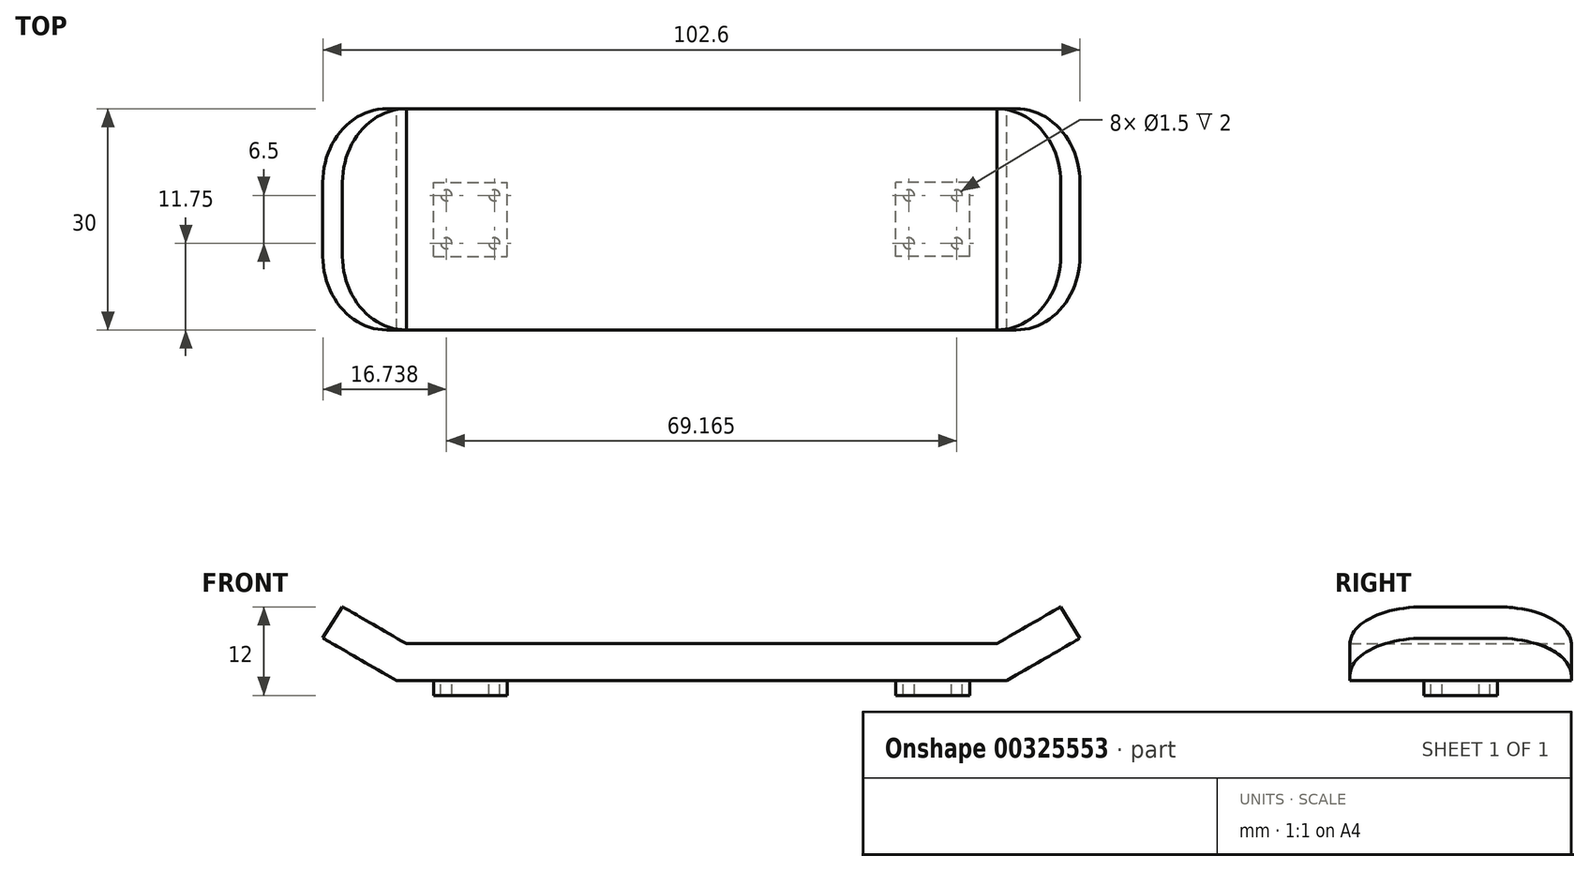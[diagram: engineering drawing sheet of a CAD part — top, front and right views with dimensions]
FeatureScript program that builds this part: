
annotation { "Feature Type Name" : "Feature", "Feature Type Description" : "" }
export const myFeature = defineFeature(function(context is Context, id is Id, definition is map)
    precondition{}
    {
        {
            var Q0;
            Q0=qCreatedBy(makeId("Front.planeOp"),FACE);
            var sketch = newSketch(context, id + "F0", { "sketchPlane" : qUnion([Q0])});
            skLineSegment(sketch, "E0", {"start": v(0, 0) * mm, "end": v(-40, 0) * mm});
            skLineSegment(sketch, "E1", {"start": v(0, 0) * mm, "end": v(40, 0) * mm});
            skLineSegment(sketch, "E2", {"start": v(40, 0) * mm, "end": v(48.66, 5) * mm});
            skLineSegment(sketch, "E3", {"start": v(-40, 0) * mm, "end": v(-48.66, 5) * mm});
            skLineSegment(sketch, "E4", {"start": v(-41.33, -5) * mm, "end": v(41.34, -5) * mm});
            skLineSegment(sketch, "E5", {"start": v(41.34, -5) * mm, "end": v(51.28, 0.74) * mm});
            skLineSegment(sketch, "E6", {"start": v(51.28, 0.74) * mm, "end": v(48.66, 5) * mm});
            skLineSegment(sketch, "E7", {"start": v(-41.33, -5) * mm, "end": v(-51.32, 0.77) * mm});
            skLineSegment(sketch, "E8", {"start": v(-51.32, 0.77) * mm, "end": v(-48.66, 5) * mm});
            skSolve(sketch);
        }
        {
            var Q0;
            Q0=makeQuery(id+"F0.imprint","IMPRINT",FACE,{"disambiguationData":[TD([[makeQuery(id+"F0.imprint","IMPRINT",EDGE,{"derivedFrom":sQuery(id+"F0.wireOp",EDGE,"E0")}),1.0]])]});
            extrude(context, id + "F1", {"entities" : qUnion([Q0]), "depth" : 30 * mm});
        }
        {
            var Q0;
            Q0=makeQuery(id+"F1.opExtrude","CAP_EDGE",EDGE,{"disambiguationData":[OSD([sQuery(id+"F0.wireOp",EDGE,"E6")])],"isStart":false});
            fillet(context, id + "F2", {"entities" : qUnion([Q0]), "radius" : 10 * mm, "tangentPropagation" : true, "allowEdgeOverflow" : false});
        }
        {
            var Q0;
            Q0=makeQuery(id+"F1.opExtrude","CAP_EDGE",EDGE,{"disambiguationData":[OSD([sQuery(id+"F0.wireOp",EDGE,"E6")])],"isStart":true});
            fillet(context, id + "F3", {"entities" : qUnion([Q0]), "radius" : 10 * mm, "tangentPropagation" : true, "allowEdgeOverflow" : false});
        }
        {
            var Q0;
            Q0=makeQuery(id+"F1.opExtrude","CAP_EDGE",EDGE,{"disambiguationData":[OSD([sQuery(id+"F0.wireOp",EDGE,"E8")])],"isStart":true});
            fillet(context, id + "F4", {"entities" : qUnion([Q0]), "radius" : 10 * mm, "tangentPropagation" : true, "allowEdgeOverflow" : false});
        }
        {
            var Q0;
            Q0=makeQuery(id+"F1.opExtrude","CAP_EDGE",EDGE,{"disambiguationData":[OSD([sQuery(id+"F0.wireOp",EDGE,"E8")])],"isStart":false});
            fillet(context, id + "F5", {"entities" : qUnion([Q0]), "radius" : 10 * mm, "tangentPropagation" : true, "allowEdgeOverflow" : false});
        }
        {
            var Q0;
            Q0=makeQuery(id+"F1.opExtrude","SWEPT_FACE",FACE,{"disambiguationData":[OSD([sQuery(id+"F0.wireOp",EDGE,"E4")])]});
            var sketch = newSketch(context, id + "F6", { "sketchPlane" : qUnion([Q0])});
            skLineSegment(sketch, "E9.bottom", {"start": v(-36.33, 20) * mm, "end": v(-26.33, 20) * mm});
            skLineSegment(sketch, "E9.top", {"start": v(-36.33, 10) * mm, "end": v(-26.33, 10) * mm});
            skLineSegment(sketch, "E9.left", {"start": v(-36.33, 20) * mm, "end": v(-36.33, 10) * mm});
            skLineSegment(sketch, "E9.right", {"start": v(-26.33, 20) * mm, "end": v(-26.33, 10) * mm});
            skCircle(sketch, "E10", {"center": v(-34.58, 18.25) * mm, "radius": 0.75 * mm});
            skCircle(sketch, "E11.MirrorC", {"center": v(-28.08, 18.25) * mm, "radius": 0.75 * mm});
            skCircle(sketch, "E12.MirrorC", {"center": v(-34.58, 11.75) * mm, "radius": 0.75 * mm});
            skCircle(sketch, "E13.MirrorC", {"center": v(-28.08, 11.75) * mm, "radius": 0.75 * mm});
            skLineSegment(sketch, "E14.MirrorCS", {"start": v(36.33, 20) * mm, "end": v(26.33, 20) * mm});
            skLineSegment(sketch, "E15.MirrorCS", {"start": v(26.33, 20) * mm, "end": v(26.33, 10) * mm});
            skLineSegment(sketch, "E16.MirrorCS", {"start": v(36.33, 10) * mm, "end": v(26.33, 10) * mm});
            skLineSegment(sketch, "E17.MirrorCS", {"start": v(36.33, 20) * mm, "end": v(36.33, 10) * mm});
            skCircle(sketch, "E18.MirrorC", {"center": v(34.58, 11.75) * mm, "radius": 0.75 * mm});
            skCircle(sketch, "E19.MirrorC", {"center": v(28.08, 11.75) * mm, "radius": 0.75 * mm});
            skCircle(sketch, "E20.MirrorC", {"center": v(28.08, 18.25) * mm, "radius": 0.75 * mm});
            skCircle(sketch, "E21.MirrorC", {"center": v(34.58, 18.25) * mm, "radius": 0.75 * mm});
            skSolve(sketch);
        }
        {
            var Q0;
            Q0=makeQuery(id+"F6.imprint","IMPRINT",FACE,{"disambiguationData":[TD([[makeQuery(id+"F6.imprint","IMPRINT",EDGE,{"derivedFrom":sQuery(id+"F6.wireOp",EDGE,"E14.MirrorCS")}),1.0]])]});
            var Q1;
            Q1=makeQuery(id+"F6.imprint","IMPRINT",FACE,{"disambiguationData":[TD([[makeQuery(id+"F6.imprint","IMPRINT",EDGE,{"derivedFrom":sQuery(id+"F6.wireOp",EDGE,"E9.bottom")}),-1.0]])]});
            extrude(context, id + "F7", {"entities" : qUnion([Q0, Q1]), "operationType" : NewBodyOperationType.ADD, "depth" : 2 * mm});
        }
    });
